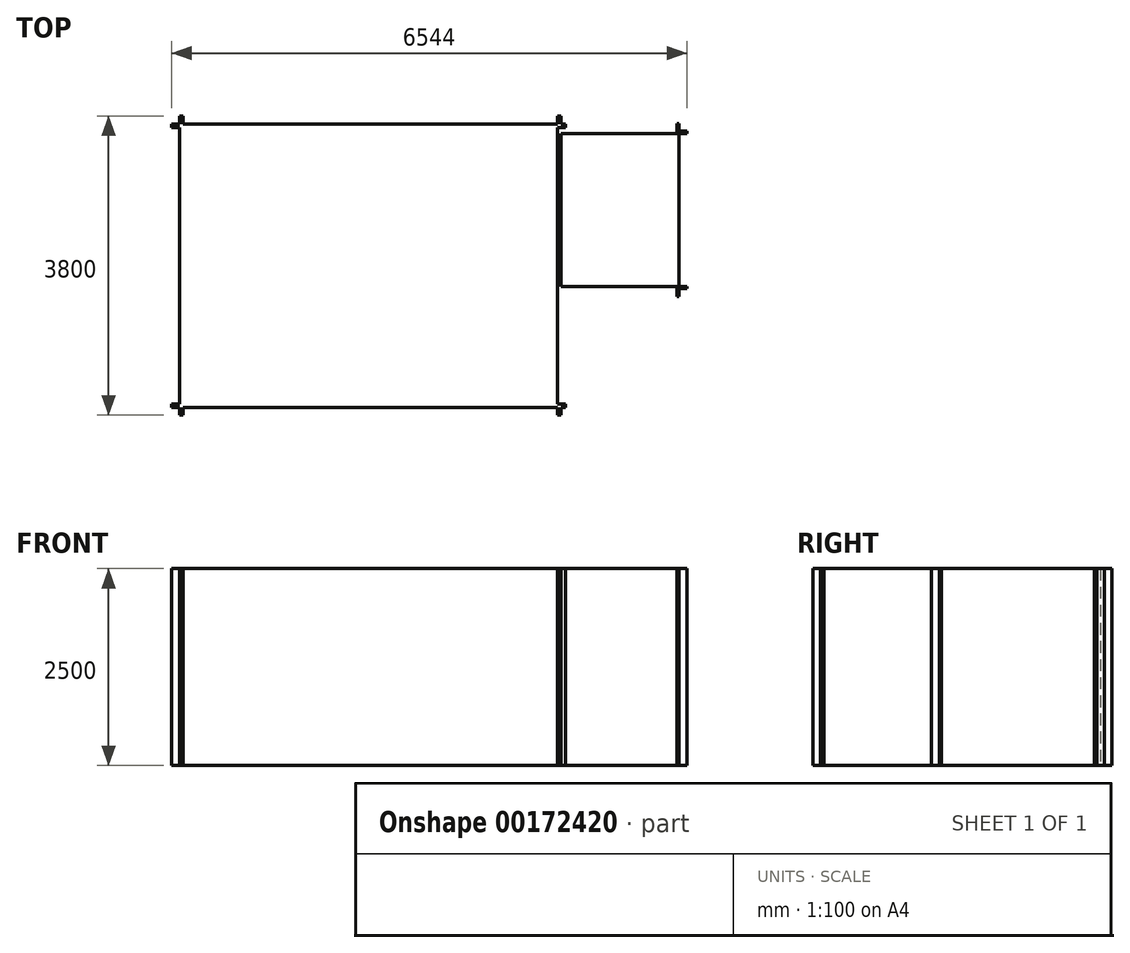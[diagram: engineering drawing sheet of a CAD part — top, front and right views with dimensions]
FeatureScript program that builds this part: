
annotation { "Feature Type Name" : "Feature", "Feature Type Description" : "" }
export const myFeature = defineFeature(function(context is Context, id is Id, definition is map)
    precondition{}
    {
        {
            var Q0;
            Q0=qCreatedBy(makeId("Top.planeOp"),FACE);
            var sketch = newSketch(context, id + "F0", { "sketchPlane" : qUnion([Q0])});
            skLineSegment(sketch, "E0.bottom", {"start": v(-5025.91, 74.86) * mm, "end": v(-25.91, 74.86) * mm});
            skLineSegment(sketch, "E0.top", {"start": v(-5025.91, 30.86) * mm, "end": v(-25.91, 30.86) * mm});
            skLineSegment(sketch, "E0.left", {"start": v(-5025.91, 74.86) * mm, "end": v(-5025.91, 30.86) * mm});
            skLineSegment(sketch, "E0.right", {"start": v(-25.91, 74.86) * mm, "end": v(-25.91, 30.86) * mm});
            skLineSegment(sketch, "E1.bottom", {"start": v(-4925.91, 174.86) * mm, "end": v(-4881.91, 174.86) * mm});
            skLineSegment(sketch, "E1.top", {"start": v(-4925.91, -3625.14) * mm, "end": v(-4881.91, -3625.14) * mm});
            skLineSegment(sketch, "E1.left", {"start": v(-4925.91, 174.86) * mm, "end": v(-4925.91, -3625.14) * mm});
            skLineSegment(sketch, "E1.right", {"start": v(-4881.91, 174.86) * mm, "end": v(-4881.91, -3625.14) * mm});
            skLineSegment(sketch, "E2.bottom", {"start": v(-125.91, 174.86) * mm, "end": v(-81.91, 174.86) * mm});
            skLineSegment(sketch, "E2.top", {"start": v(-125.91, -3625.14) * mm, "end": v(-81.91, -3625.14) * mm});
            skLineSegment(sketch, "E2.left", {"start": v(-125.91, 174.86) * mm, "end": v(-125.91, -3625.14) * mm});
            skLineSegment(sketch, "E2.right", {"start": v(-81.91, 174.86) * mm, "end": v(-81.91, -3625.14) * mm});
            skLineSegment(sketch, "E3.bottom", {"start": v(-5025.91, -3481.14) * mm, "end": v(-25.91, -3481.14) * mm});
            skLineSegment(sketch, "E3.top", {"start": v(-5025.91, -3525.14) * mm, "end": v(-25.91, -3525.14) * mm});
            skLineSegment(sketch, "E3.left", {"start": v(-5025.91, -3481.14) * mm, "end": v(-5025.91, -3525.14) * mm});
            skLineSegment(sketch, "E3.right", {"start": v(-25.91, -3481.14) * mm, "end": v(-25.91, -3525.14) * mm});
            skLineSegment(sketch, "E4.bottom", {"start": v(1390.09, 80.86) * mm, "end": v(1418.09, 80.86) * mm});
            skLineSegment(sketch, "E4.top", {"start": v(1390.09, -2119.14) * mm, "end": v(1418.09, -2119.14) * mm});
            skLineSegment(sketch, "E4.left", {"start": v(1390.09, 80.86) * mm, "end": v(1390.09, -2119.14) * mm});
            skLineSegment(sketch, "E4.right", {"start": v(1418.09, 80.86) * mm, "end": v(1418.09, -2119.14) * mm});
            skLineSegment(sketch, "E5.bottom", {"start": v(-81.91, -19.14) * mm, "end": v(1518.09, -19.14) * mm});
            skLineSegment(sketch, "E5.top", {"start": v(-81.91, -47.14) * mm, "end": v(1518.09, -47.14) * mm});
            skLineSegment(sketch, "E5.left", {"start": v(-81.91, -19.14) * mm, "end": v(-81.91, -47.14) * mm});
            skLineSegment(sketch, "E5.right", {"start": v(1518.09, -19.14) * mm, "end": v(1518.09, -47.14) * mm});
            skLineSegment(sketch, "E6.bottom", {"start": v(-81.91, -1991.14) * mm, "end": v(1518.09, -1991.14) * mm});
            skLineSegment(sketch, "E6.top", {"start": v(-81.91, -2019.14) * mm, "end": v(1518.09, -2019.14) * mm});
            skLineSegment(sketch, "E6.left", {"start": v(-81.91, -1991.14) * mm, "end": v(-81.91, -2019.14) * mm});
            skLineSegment(sketch, "E6.right", {"start": v(1518.09, -1991.14) * mm, "end": v(1518.09, -2019.14) * mm});
            skSolve(sketch);
        }
        {
            var Q0;
            {var subQ0=sQuery(id+"F0.wireOp",EDGE,"E5.left");Q0=makeQuery(id+"F0.imprint","IMPRINT",FACE,{"disambiguationData":[TD([[makeQuery(id+"F0.imprint","IMPRINT",EDGE,{"derivedFrom":subQ0}),-1.0]])]});}
            var Q1;
            {var subQ0=sQuery(id+"F0.wireOp",EDGE,"E1.right");var subQ1=sQuery(id+"F0.wireOp",EDGE,"E0.top");var subQ2=makeQuery(id+"F0.imprint","INTERSECT",VERTEX,{"derivedFrom":[subQ1,subQ0]});Q1=makeQuery(id+"F0.imprint","IMPRINT",FACE,{"disambiguationData":[TD([[makeQuery(id+"F0.imprint","IMPRINT",EDGE,{"disambiguationData":[TD([[subQ2,-1.0]])],"derivedFrom":subQ1}),-1.0]])]});}
            var Q2;
            {var subQ0=sQuery(id+"F0.wireOp",EDGE,"E1.left");var subQ1=sQuery(id+"F0.wireOp",EDGE,"E0.top");var subQ2=makeQuery(id+"F0.imprint","INTERSECT",VERTEX,{"derivedFrom":[subQ1,subQ0]});Q2=makeQuery(id+"F0.imprint","IMPRINT",FACE,{"disambiguationData":[TD([[makeQuery(id+"F0.imprint","IMPRINT",EDGE,{"disambiguationData":[TD([[subQ2,-1.0]])],"derivedFrom":subQ1}),-1.0]])]});}
            var Q3;
            {var subQ0=sQuery(id+"F0.wireOp",EDGE,"E5.top");var subQ5=sQuery(id+"F0.wireOp",EDGE,"E4.left");var subQ6=makeQuery(id+"F0.imprint","INTERSECT",VERTEX,{"derivedFrom":[subQ5,subQ0]});Q3=makeQuery(id+"F0.imprint","IMPRINT",FACE,{"disambiguationData":[TD([[makeQuery(id+"F0.imprint","IMPRINT",EDGE,{"disambiguationData":[TD([[subQ6,-1.0]])],"derivedFrom":subQ5}),-1.0]])]});}
            var Q4;
            {var subQ0=sQuery(id+"F0.wireOp",EDGE,"E5.bottom");var subQ1=sQuery(id+"F0.wireOp",EDGE,"E4.left");var subQ2=makeQuery(id+"F0.imprint","INTERSECT",VERTEX,{"derivedFrom":[subQ1,subQ0]});Q4=makeQuery(id+"F0.imprint","IMPRINT",FACE,{"disambiguationData":[TD([[makeQuery(id+"F0.imprint","IMPRINT",EDGE,{"disambiguationData":[TD([[subQ2,-1.0]])],"derivedFrom":subQ1}),1.0]])]});}
            var Q5;
            {var subQ0=sQuery(id+"F0.wireOp",EDGE,"E3.top");var subQ1=sQuery(id+"F0.wireOp",EDGE,"E2.left");var subQ2=makeQuery(id+"F0.imprint","INTERSECT",VERTEX,{"derivedFrom":[subQ1,subQ0]});Q5=makeQuery(id+"F0.imprint","IMPRINT",FACE,{"disambiguationData":[TD([[makeQuery(id+"F0.imprint","IMPRINT",EDGE,{"disambiguationData":[TD([[subQ2,1.0]])],"derivedFrom":subQ1}),1.0]])]});}
            var Q6;
            {var subQ0=sQuery(id+"F0.wireOp",EDGE,"E1.left");var subQ1=sQuery(id+"F0.wireOp",EDGE,"E0.bottom");var subQ2=makeQuery(id+"F0.imprint","INTERSECT",VERTEX,{"derivedFrom":[subQ1,subQ0]});Q6=makeQuery(id+"F0.imprint","IMPRINT",FACE,{"disambiguationData":[TD([[makeQuery(id+"F0.imprint","IMPRINT",EDGE,{"disambiguationData":[TD([[subQ2,-1.0]])],"derivedFrom":subQ1}),-1.0]])]});}
            var Q7;
            {var subQ0=sQuery(id+"F0.wireOp",EDGE,"E5.top");var subQ1=sQuery(id+"F0.wireOp",EDGE,"E4.left");var subQ2=makeQuery(id+"F0.imprint","INTERSECT",VERTEX,{"derivedFrom":[subQ1,subQ0]});Q7=makeQuery(id+"F0.imprint","IMPRINT",FACE,{"disambiguationData":[TD([[makeQuery(id+"F0.imprint","IMPRINT",EDGE,{"disambiguationData":[TD([[subQ2,-1.0]])],"derivedFrom":subQ1}),1.0]])]});}
            var Q8;
            {var subQ5=sQuery(id+"F0.wireOp",EDGE,"E5.left");Q8=makeQuery(id+"F0.imprint","IMPRINT",FACE,{"disambiguationData":[TD([[makeQuery(id+"F0.imprint","IMPRINT",EDGE,{"derivedFrom":subQ5}),1.0]])]});}
            var Q9;
            {var subQ0=sQuery(id+"F0.wireOp",EDGE,"E6.top");var subQ1=sQuery(id+"F0.wireOp",EDGE,"E4.left");var subQ2=makeQuery(id+"F0.imprint","INTERSECT",VERTEX,{"derivedFrom":[subQ1,subQ0]});Q9=makeQuery(id+"F0.imprint","IMPRINT",FACE,{"disambiguationData":[TD([[makeQuery(id+"F0.imprint","IMPRINT",EDGE,{"disambiguationData":[TD([[subQ2,1.0]])],"derivedFrom":subQ1}),1.0]])]});}
            var Q10;
            {var subQ0=sQuery(id+"F0.wireOp",EDGE,"E3.top");var subQ1=sQuery(id+"F0.wireOp",EDGE,"E1.right");var subQ2=makeQuery(id+"F0.imprint","INTERSECT",VERTEX,{"derivedFrom":[subQ1,subQ0]});Q10=makeQuery(id+"F0.imprint","IMPRINT",FACE,{"disambiguationData":[TD([[makeQuery(id+"F0.imprint","IMPRINT",EDGE,{"disambiguationData":[TD([[subQ2,1.0]])],"derivedFrom":subQ1}),1.0]])]});}
            var Q11;
            {var subQ0=sQuery(id+"F0.wireOp",EDGE,"E0.left");Q11=makeQuery(id+"F0.imprint","IMPRINT",FACE,{"disambiguationData":[TD([[makeQuery(id+"F0.imprint","IMPRINT",EDGE,{"derivedFrom":subQ0}),1.0]])]});}
            var Q12;
            {var subQ0=sQuery(id+"F0.wireOp",EDGE,"E3.bottom");var subQ1=sQuery(id+"F0.wireOp",EDGE,"E1.left");var subQ2=makeQuery(id+"F0.imprint","INTERSECT",VERTEX,{"derivedFrom":[subQ1,subQ0]});Q12=makeQuery(id+"F0.imprint","IMPRINT",FACE,{"disambiguationData":[TD([[makeQuery(id+"F0.imprint","IMPRINT",EDGE,{"disambiguationData":[TD([[subQ2,-1.0]])],"derivedFrom":subQ1}),1.0]])]});}
            var Q13;
            {var subQ5=sQuery(id+"F0.wireOp",EDGE,"E3.left");Q13=makeQuery(id+"F0.imprint","IMPRINT",FACE,{"disambiguationData":[TD([[makeQuery(id+"F0.imprint","IMPRINT",EDGE,{"derivedFrom":subQ5}),1.0]])]});}
            var Q14;
            {var subQ5=sQuery(id+"F0.wireOp",EDGE,"E6.left");Q14=makeQuery(id+"F0.imprint","IMPRINT",FACE,{"disambiguationData":[TD([[makeQuery(id+"F0.imprint","IMPRINT",EDGE,{"derivedFrom":subQ5}),1.0]])]});}
            var Q15;
            {var subQ5=sQuery(id+"F0.wireOp",EDGE,"E5.right");Q15=makeQuery(id+"F0.imprint","IMPRINT",FACE,{"disambiguationData":[TD([[makeQuery(id+"F0.imprint","IMPRINT",EDGE,{"derivedFrom":subQ5}),-1.0]])]});}
            var Q16;
            {var subQ5=sQuery(id+"F0.wireOp",EDGE,"E6.right");Q16=makeQuery(id+"F0.imprint","IMPRINT",FACE,{"disambiguationData":[TD([[makeQuery(id+"F0.imprint","IMPRINT",EDGE,{"derivedFrom":subQ5}),-1.0]])]});}
            var Q17;
            {var subQ0=sQuery(id+"F0.wireOp",EDGE,"E1.right");var subQ1=sQuery(id+"F0.wireOp",EDGE,"E0.bottom");var subQ2=makeQuery(id+"F0.imprint","INTERSECT",VERTEX,{"derivedFrom":[subQ1,subQ0]});Q17=makeQuery(id+"F0.imprint","IMPRINT",FACE,{"disambiguationData":[TD([[makeQuery(id+"F0.imprint","IMPRINT",EDGE,{"disambiguationData":[TD([[subQ2,-1.0]])],"derivedFrom":subQ1}),-1.0]])]});}
            var Q18;
            {var subQ5=sQuery(id+"F0.wireOp",EDGE,"E1.bottom");Q18=makeQuery(id+"F0.imprint","IMPRINT",FACE,{"disambiguationData":[TD([[makeQuery(id+"F0.imprint","IMPRINT",EDGE,{"derivedFrom":subQ5}),-1.0]])]});}
            var Q19;
            {var subQ5=sQuery(id+"F0.wireOp",EDGE,"E2.bottom");Q19=makeQuery(id+"F0.imprint","IMPRINT",FACE,{"disambiguationData":[TD([[makeQuery(id+"F0.imprint","IMPRINT",EDGE,{"derivedFrom":subQ5}),-1.0]])]});}
            var Q20;
            {var subQ0=sQuery(id+"F0.wireOp",EDGE,"E2.left");var subQ1=sQuery(id+"F0.wireOp",EDGE,"E0.bottom");var subQ2=makeQuery(id+"F0.imprint","INTERSECT",VERTEX,{"derivedFrom":[subQ1,subQ0]});Q20=makeQuery(id+"F0.imprint","IMPRINT",FACE,{"disambiguationData":[TD([[makeQuery(id+"F0.imprint","IMPRINT",EDGE,{"disambiguationData":[TD([[subQ2,-1.0]])],"derivedFrom":subQ1}),-1.0]])]});}
            var Q21;
            {var subQ0=sQuery(id+"F0.wireOp",EDGE,"E1.top");Q21=makeQuery(id+"F0.imprint","IMPRINT",FACE,{"disambiguationData":[TD([[makeQuery(id+"F0.imprint","IMPRINT",EDGE,{"derivedFrom":subQ0}),1.0]])]});}
            var Q22;
            {var subQ0=sQuery(id+"F0.wireOp",EDGE,"E2.top");Q22=makeQuery(id+"F0.imprint","IMPRINT",FACE,{"disambiguationData":[TD([[makeQuery(id+"F0.imprint","IMPRINT",EDGE,{"derivedFrom":subQ0}),1.0]])]});}
            var Q23;
            {var subQ5=sQuery(id+"F0.wireOp",EDGE,"E3.right");Q23=makeQuery(id+"F0.imprint","IMPRINT",FACE,{"disambiguationData":[TD([[makeQuery(id+"F0.imprint","IMPRINT",EDGE,{"derivedFrom":subQ5}),-1.0]])]});}
            var Q24;
            {var subQ0=sQuery(id+"F0.wireOp",EDGE,"E4.bottom");Q24=makeQuery(id+"F0.imprint","IMPRINT",FACE,{"disambiguationData":[TD([[makeQuery(id+"F0.imprint","IMPRINT",EDGE,{"derivedFrom":subQ0}),-1.0]])]});}
            var Q25;
            {var subQ0=sQuery(id+"F0.wireOp",EDGE,"E4.top");Q25=makeQuery(id+"F0.imprint","IMPRINT",FACE,{"disambiguationData":[TD([[makeQuery(id+"F0.imprint","IMPRINT",EDGE,{"derivedFrom":subQ0}),1.0]])]});}
            var Q26;
            {var subQ0=sQuery(id+"F0.wireOp",EDGE,"E0.right");Q26=makeQuery(id+"F0.imprint","IMPRINT",FACE,{"disambiguationData":[TD([[makeQuery(id+"F0.imprint","IMPRINT",EDGE,{"derivedFrom":subQ0}),-1.0]])]});}
            extrude(context, id + "F1", {"entities" : qUnion([Q0, Q1, Q2, Q3, Q4, Q5, Q6, Q7, Q8, Q9, Q10, Q11, Q12, Q13, Q14, Q15, Q16, Q17, Q18, Q19, Q20, Q21, Q22, Q23, Q24, Q25, Q26]), "depth" : 2500 * mm});
        }
    });
